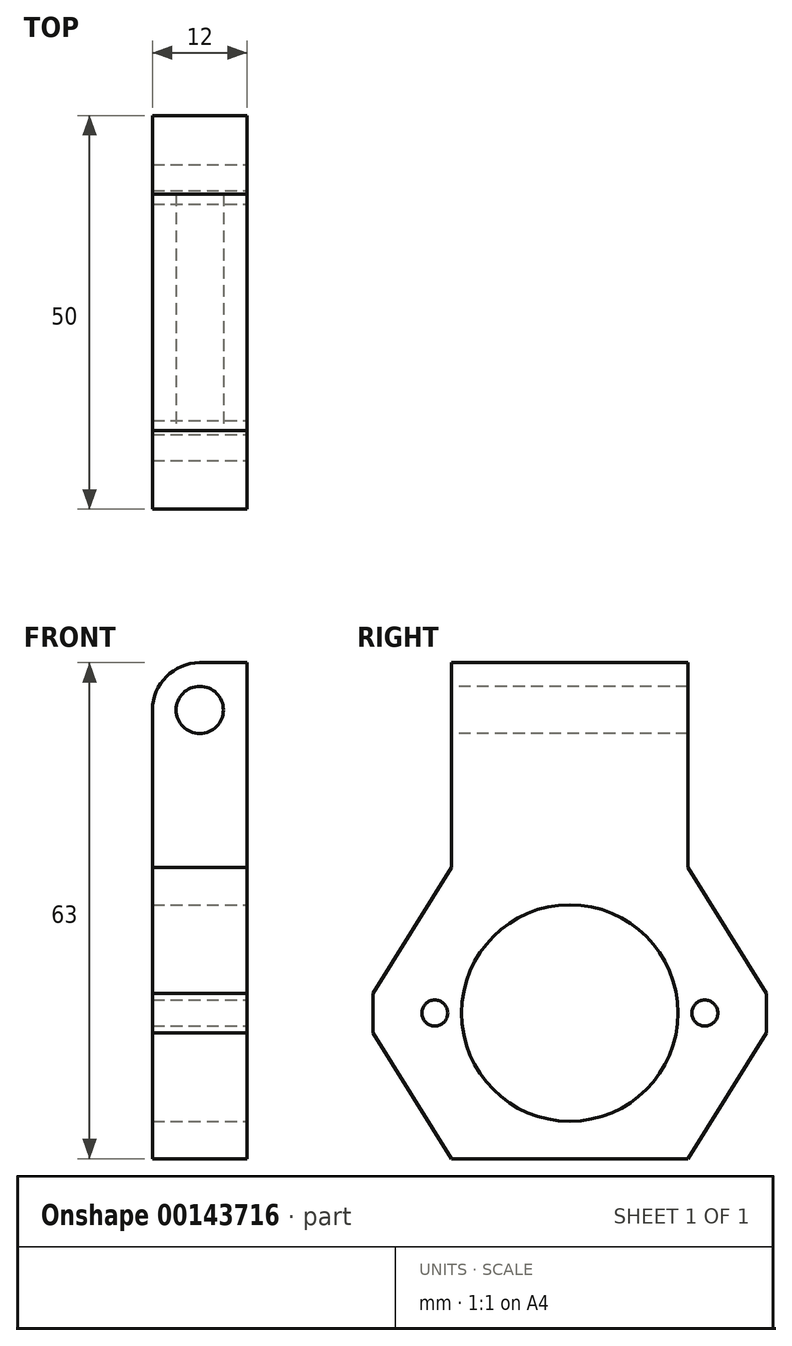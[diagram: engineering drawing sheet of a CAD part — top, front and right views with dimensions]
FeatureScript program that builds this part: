
annotation { "Feature Type Name" : "Feature", "Feature Type Description" : "" }
export const myFeature = defineFeature(function(context is Context, id is Id, definition is map)
    precondition{}
    {
        {
            var Q0;
            Q0=qCreatedBy(makeId("Right.planeOp"),FACE);
            var sketch = newSketch(context, id + "F0", { "sketchPlane" : qUnion([Q0])});
            skLineSegment(sketch, "E0", {"start": v(0, 112.01) * mm, "end": v(0, -98.38) * mm, "construction": true});
            skLineSegment(sketch, "E1", {"start": v(0, 44.5) * mm, "end": v(15, 44.5) * mm});
            skLineSegment(sketch, "E2", {"start": v(15, 44.5) * mm, "end": v(15, 18.5) * mm});
            skLineSegment(sketch, "E3", {"start": v(15, 18.5) * mm, "end": v(25, 2.5) * mm});
            skLineSegment(sketch, "E4", {"start": v(25, 2.5) * mm, "end": v(25, -2.5) * mm});
            skLineSegment(sketch, "E5", {"start": v(25, -2.5) * mm, "end": v(15, -18.5) * mm});
            skLineSegment(sketch, "E6", {"start": v(15, -18.5) * mm, "end": v(0, -18.5) * mm});
            skArc(sketch, "E7", {"start": v(0, -13.75) * mm, "mid": v(13.75, 0) * mm, "end": v(0, 13.75) * mm});
            skLineSegment(sketch, "E8.MirrorCS", {"start": v(-15, 44.5) * mm, "end": v(-15, 18.5) * mm});
            skLineSegment(sketch, "E9.MirrorCS", {"start": v(-15, -18.5) * mm, "end": v(0, -18.5) * mm});
            skLineSegment(sketch, "E10.MirrorCS", {"start": v(-15, 18.5) * mm, "end": v(-25, 2.5) * mm});
            skLineSegment(sketch, "E11.MirrorCS", {"start": v(-25, -2.5) * mm, "end": v(-15, -18.5) * mm});
            skArc(sketch, "E12.MirrorCS", {"start": v(0, -13.75) * mm, "mid": v(-13.75, 0) * mm, "end": v(0, 13.75) * mm});
            skLineSegment(sketch, "E13.MirrorCS", {"start": v(0, 44.5) * mm, "end": v(-15, 44.5) * mm});
            skLineSegment(sketch, "E14.MirrorCS", {"start": v(-25, 2.5) * mm, "end": v(-25, -2.5) * mm});
            skSolve(sketch);
        }
        {
            var Q0;
            Q0=makeQuery(id+"F0.imprint","IMPRINT",FACE,{"disambiguationData":[TD([[makeQuery(id+"F0.imprint","IMPRINT",EDGE,{"derivedFrom":sQuery(id+"F0.wireOp",EDGE,"E1")}),-1.0]])]});
            extrude(context, id + "F1", {"entities" : qUnion([Q0]), "oppositeDirection" : true, "depth" : 12 * mm});
        }
        {
            var Q0;
            Q0=qCreatedBy(makeId("Right.planeOp"),FACE);
            var sketch = newSketch(context, id + "F2", { "sketchPlane" : qUnion([Q0])});
            skPoint(sketch, "E15", {"position": v(17.15, 0) * mm});
            skPoint(sketch, "E16", {"position": v(-17.15, 0) * mm});
            skSolve(sketch);
        }
        {
            var Q0;
            Q0=sQuery(id+"F2.wireOp",VERTEX,"E16");
            var Q1;
            Q1=sQuery(id+"F2.wireOp",VERTEX,"E15");
            var Q2;
            Q2=makeQuery(id+"F1.opExtrude","SWEPT_BODY",BODY,{"disambiguationData":[OSD([sQuery(id+"F0.wireOp",EDGE,"E1"),sQuery(id+"F0.wireOp",EDGE,"E2"),sQuery(id+"F0.wireOp",EDGE,"E3"),sQuery(id+"F0.wireOp",EDGE,"E4"),sQuery(id+"F0.wireOp",EDGE,"E5"),sQuery(id+"F0.wireOp",EDGE,"E6"),sQuery(id+"F0.wireOp",EDGE,"E7"),sQuery(id+"F0.wireOp",EDGE,"E8.MirrorCS"),sQuery(id+"F0.wireOp",EDGE,"E9.MirrorCS"),sQuery(id+"F0.wireOp",EDGE,"E10.MirrorCS"),sQuery(id+"F0.wireOp",EDGE,"E11.MirrorCS"),sQuery(id+"F0.wireOp",EDGE,"E12.MirrorCS"),sQuery(id+"F0.wireOp",EDGE,"E13.MirrorCS"),sQuery(id+"F0.wireOp",EDGE,"E14.MirrorCS")])]});
            hole(context, id + "F3", {"style" : HoleStyle.SIMPLE, "endStyle" : HoleEndStyle.THROUGH, "standardTappedOrClearance" : lookupTablePath({ "standard" : "ISO", "fit" : "Normal", "size" : "M3", "type" : "Clearance" }), "standardBlindInLast" : lookupTablePath({ "fit" : "Standard", "standard" : "ISO", "size" : "M3", "type" : "Clearance" }), "holeDiameter" : 3.3 * mm, "locations" : qUnion([Q0, Q1]), "scope" : qUnion([Q2]), "isTappedThrough" : true});
        }
        {
            var Q0;
            Q0=makeQuery(id+"F1.opExtrude","SWEPT_FACE",FACE,{"disambiguationData":[OSD([sQuery(id+"F0.wireOp",EDGE,"E8.MirrorCS")])]});
            var sketch = newSketch(context, id + "F4", { "sketchPlane" : qUnion([Q0])});
            skCircle(sketch, "E17", {"center": v(-6, 38.5) * mm, "radius": 3 * mm});
            skSolve(sketch);
        }
        {
            var Q0;
            Q0=makeQuery(id+"F4.imprint","IMPRINT",FACE,{"disambiguationData":[TD([[makeQuery(id+"F4.imprint","IMPRINT",EDGE,{"derivedFrom":sQuery(id+"F4.wireOp",EDGE,"E17")}),1.0]])]});
            var Q1;
            Q1=sQuery(id+"F4.wireOp",EDGE,"E17");
            extrude(context, id + "F5", {"entities" : qUnion([Q0]), "operationType" : NewBodyOperationType.REMOVE, "surfaceEntities" : qUnion([Q1]), "endBound" : BoundingType.UP_TO_NEXT, "oppositeDirection" : true, "depth" : 25 * mm});
        }
        {
            var Q0;
            Q0=makeQuery(id+"F1.opExtrude","CAP_EDGE",EDGE,{"disambiguationData":[OSD([sQuery(id+"F0.wireOp",EDGE,"E1"),sQuery(id+"F0.wireOp",EDGE,"E13.MirrorCS")])],"isStart":false});
            fillet(context, id + "F6", {"entities" : qUnion([Q0]), "radius" : 6 * mm, "tangentPropagation" : true, "allowEdgeOverflow" : false});
        }
    });
